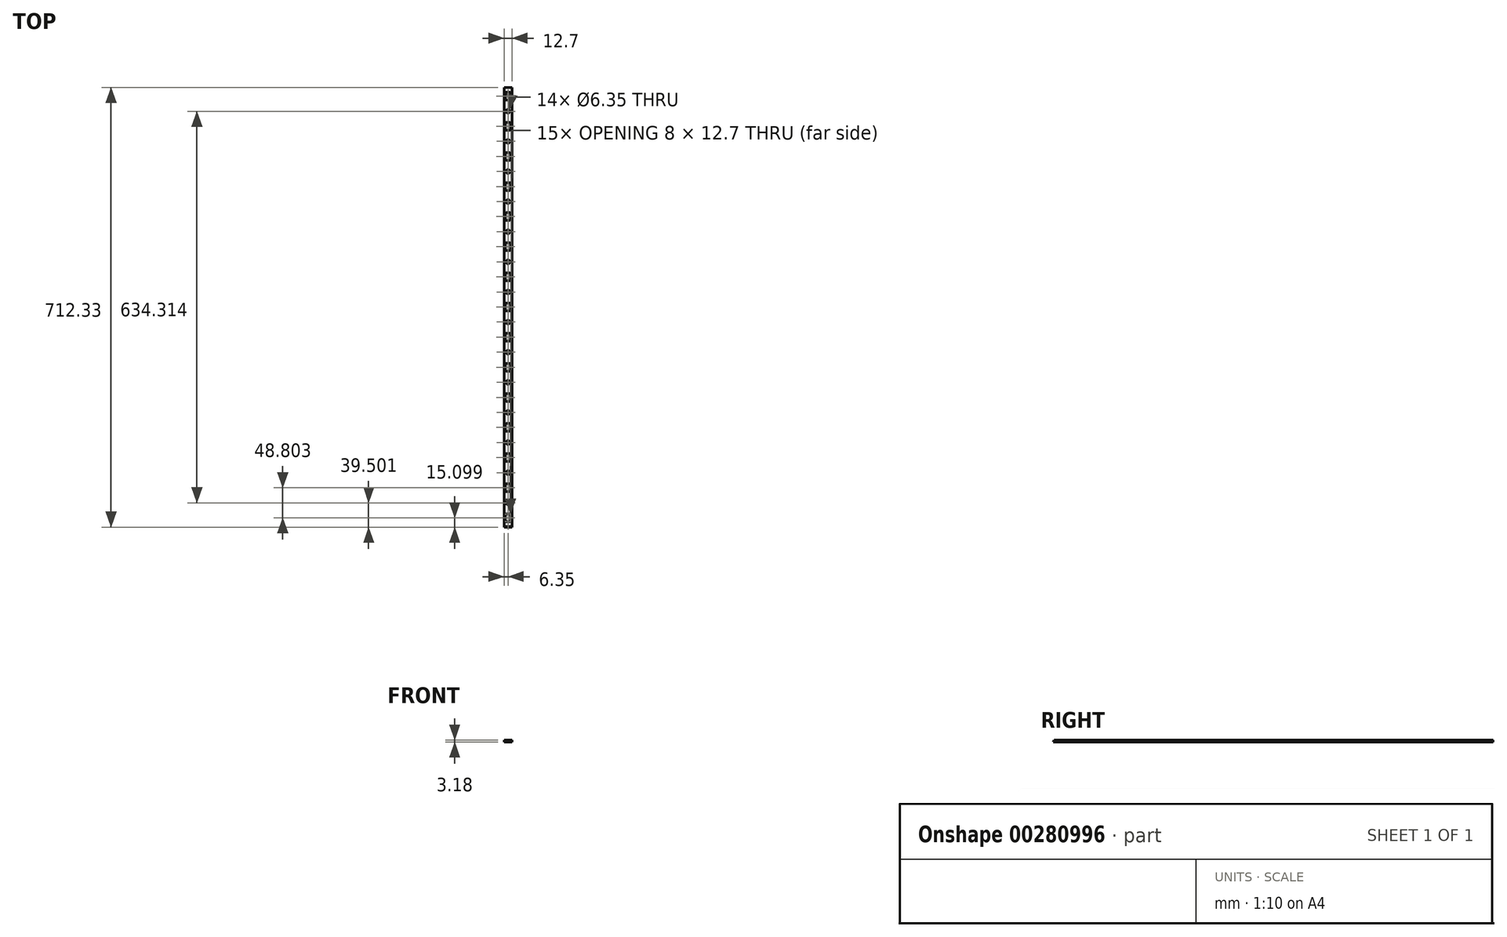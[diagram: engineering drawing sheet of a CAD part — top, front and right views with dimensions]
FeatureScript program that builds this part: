
annotation { "Feature Type Name" : "Feature", "Feature Type Description" : "" }
export const myFeature = defineFeature(function(context is Context, id is Id, definition is map)
    precondition{}
    {
        {
            var Q0;
            Q0=qCreatedBy(makeId("Right.planeOp"),FACE);
            var sketch = newSketch(context, id + "F0", { "sketchPlane" : qUnion([Q0])});
            skLineSegment(sketch, "E0", {"start": v(0, 0) * mm, "end": v(1.13, 3.17) * mm});
            skLineSegment(sketch, "E1", {"start": v(1.13, 3.18) * mm, "end": v(712.33, 3.18) * mm});
            skLineSegment(sketch, "E2", {"start": v(0, 0) * mm, "end": v(712.33, 0) * mm});
            skLineSegment(sketch, "E3", {"start": v(712.33, 3.18) * mm, "end": v(712.33, 0) * mm});
            skSolve(sketch);
        }
        {
            var Q0;
            Q0 = qSketchRegion(id + "F0", true);
            extrude(context, id + "F1", {"entities" : qUnion([Q0]), "oppositeDirection" : true, "depth" : 12.7 * mm});
        }
        {
            var Q0;
            Q0=makeQuery(id+"F1.opExtrude","SWEPT_FACE",FACE,{"disambiguationData":[OSD([sQuery(id+"F0.wireOp",EDGE,"E1")])]});
            var sketch = newSketch(context, id + "F2", { "sketchPlane" : qUnion([Q0])});
            skLineSegment(sketch, "E4.bottom", {"start": v(-3.62, 8.75) * mm, "end": v(-9.08, 8.75) * mm});
            skLineSegment(sketch, "E4.top", {"start": v(-3.62, 21.45) * mm, "end": v(-9.08, 21.45) * mm});
            skLineSegment(sketch, "E4.left", {"start": v(-2.35, 10.02) * mm, "end": v(-2.35, 20.18) * mm});
            skLineSegment(sketch, "E4.right", {"start": v(-10.35, 10.02) * mm, "end": v(-10.35, 20.18) * mm});
            skPoint(sketch, "E4.middle", {"position": v(-6.35, 15.1) * mm});
            skPoint(sketch, "E4.middle.positionSnap0", {"position": v(-6.35, 1.13) * mm});
            skPoint(sketch, "E4.centerSnap0", {"position": v(-6.35, 1.13) * mm});
            skPoint(sketch, "E5.visualSharp", {"position": v(-2.35, 21.45) * mm});
            skArc(sketch, "E5.filletArc", {"start": v(-2.35, 20.18) * mm, "mid": v(-2.72, 21.08) * mm, "end": v(-3.62, 21.45) * mm});
            skPoint(sketch, "E6.visualSharp", {"position": v(-10.35, 21.45) * mm});
            skArc(sketch, "E6.filletArc", {"start": v(-9.08, 21.45) * mm, "mid": v(-9.98, 21.08) * mm, "end": v(-10.35, 20.18) * mm});
            skPoint(sketch, "E7.visualSharp", {"position": v(-2.35, 8.75) * mm});
            skArc(sketch, "E7.filletArc", {"start": v(-3.62, 8.75) * mm, "mid": v(-2.72, 9.12) * mm, "end": v(-2.35, 10.02) * mm});
            skPoint(sketch, "E8.visualSharp", {"position": v(-10.35, 8.75) * mm});
            skArc(sketch, "E8.filletArc", {"start": v(-10.35, 10.02) * mm, "mid": v(-9.98, 9.12) * mm, "end": v(-9.08, 8.75) * mm});
            skArc(sketch, "E9.0.1.0", {"start": v(-3.62, 57.55) * mm, "mid": v(-2.72, 57.92) * mm, "end": v(-2.35, 58.82) * mm});
            skLineSegment(sketch, "E9.0.1.1", {"start": v(-10.35, 58.82) * mm, "end": v(-10.35, 68.98) * mm});
            skLineSegment(sketch, "E9.0.1.2", {"start": v(-3.62, 57.55) * mm, "end": v(-9.08, 57.55) * mm});
            skLineSegment(sketch, "E9.0.1.3", {"start": v(-2.35, 58.82) * mm, "end": v(-2.35, 68.98) * mm});
            skArc(sketch, "E9.0.1.4", {"start": v(-2.35, 68.98) * mm, "mid": v(-2.72, 69.88) * mm, "end": v(-3.62, 70.25) * mm});
            skLineSegment(sketch, "E9.0.1.5", {"start": v(-3.62, 70.25) * mm, "end": v(-9.08, 70.25) * mm});
            skArc(sketch, "E9.0.1.6", {"start": v(-9.08, 70.25) * mm, "mid": v(-9.98, 69.88) * mm, "end": v(-10.35, 68.98) * mm});
            skArc(sketch, "E9.0.1.7", {"start": v(-10.35, 58.82) * mm, "mid": v(-9.98, 57.92) * mm, "end": v(-9.08, 57.55) * mm});
            skArc(sketch, "E9.0.2.0", {"start": v(-3.62, 106.36) * mm, "mid": v(-2.72, 106.73) * mm, "end": v(-2.35, 107.63) * mm});
            skLineSegment(sketch, "E9.0.2.1", {"start": v(-10.35, 107.63) * mm, "end": v(-10.35, 117.79) * mm});
            skLineSegment(sketch, "E9.0.2.2", {"start": v(-3.62, 106.36) * mm, "end": v(-9.08, 106.36) * mm});
            skLineSegment(sketch, "E9.0.2.3", {"start": v(-2.35, 107.63) * mm, "end": v(-2.35, 117.79) * mm});
            skArc(sketch, "E9.0.2.4", {"start": v(-2.35, 117.79) * mm, "mid": v(-2.72, 118.68) * mm, "end": v(-3.62, 119.06) * mm});
            skLineSegment(sketch, "E9.0.2.5", {"start": v(-3.62, 119.06) * mm, "end": v(-9.08, 119.06) * mm});
            skArc(sketch, "E9.0.2.6", {"start": v(-9.08, 119.06) * mm, "mid": v(-9.98, 118.68) * mm, "end": v(-10.35, 117.79) * mm});
            skArc(sketch, "E9.0.2.7", {"start": v(-10.35, 107.63) * mm, "mid": v(-9.98, 106.73) * mm, "end": v(-9.08, 106.36) * mm});
            skArc(sketch, "E9.0.3.0", {"start": v(-3.62, 155.16) * mm, "mid": v(-2.72, 155.53) * mm, "end": v(-2.35, 156.43) * mm});
            skLineSegment(sketch, "E9.0.3.1", {"start": v(-10.35, 156.43) * mm, "end": v(-10.35, 166.59) * mm});
            skLineSegment(sketch, "E9.0.3.2", {"start": v(-3.62, 155.16) * mm, "end": v(-9.08, 155.16) * mm});
            skLineSegment(sketch, "E9.0.3.3", {"start": v(-2.35, 156.43) * mm, "end": v(-2.35, 166.59) * mm});
            skArc(sketch, "E9.0.3.4", {"start": v(-2.35, 166.59) * mm, "mid": v(-2.72, 167.49) * mm, "end": v(-3.62, 167.86) * mm});
            skLineSegment(sketch, "E9.0.3.5", {"start": v(-3.62, 167.86) * mm, "end": v(-9.08, 167.86) * mm});
            skArc(sketch, "E9.0.3.6", {"start": v(-9.08, 167.86) * mm, "mid": v(-9.98, 167.49) * mm, "end": v(-10.35, 166.59) * mm});
            skArc(sketch, "E9.0.3.7", {"start": v(-10.35, 156.43) * mm, "mid": v(-9.98, 155.53) * mm, "end": v(-9.08, 155.16) * mm});
            skArc(sketch, "E9.0.4.0", {"start": v(-3.62, 203.96) * mm, "mid": v(-2.72, 204.34) * mm, "end": v(-2.35, 205.23) * mm});
            skLineSegment(sketch, "E9.0.4.1", {"start": v(-10.35, 205.23) * mm, "end": v(-10.35, 215.4) * mm});
            skLineSegment(sketch, "E9.0.4.2", {"start": v(-3.62, 203.96) * mm, "end": v(-9.08, 203.96) * mm});
            skLineSegment(sketch, "E9.0.4.3", {"start": v(-2.35, 205.23) * mm, "end": v(-2.35, 215.4) * mm});
            skArc(sketch, "E9.0.4.4", {"start": v(-2.35, 215.4) * mm, "mid": v(-2.72, 216.3) * mm, "end": v(-3.62, 216.66) * mm});
            skLineSegment(sketch, "E9.0.4.5", {"start": v(-3.62, 216.66) * mm, "end": v(-9.08, 216.66) * mm});
            skArc(sketch, "E9.0.4.6", {"start": v(-9.08, 216.66) * mm, "mid": v(-9.98, 216.3) * mm, "end": v(-10.35, 215.4) * mm});
            skArc(sketch, "E9.0.4.7", {"start": v(-10.35, 205.23) * mm, "mid": v(-9.98, 204.34) * mm, "end": v(-9.08, 203.96) * mm});
            skArc(sketch, "E9.0.5.0", {"start": v(-3.62, 252.77) * mm, "mid": v(-2.72, 253.14) * mm, "end": v(-2.35, 254.04) * mm});
            skLineSegment(sketch, "E9.0.5.1", {"start": v(-10.35, 254.04) * mm, "end": v(-10.35, 264.2) * mm});
            skLineSegment(sketch, "E9.0.5.2", {"start": v(-3.62, 252.77) * mm, "end": v(-9.08, 252.77) * mm});
            skLineSegment(sketch, "E9.0.5.3", {"start": v(-2.35, 254.04) * mm, "end": v(-2.35, 264.2) * mm});
            skArc(sketch, "E9.0.5.4", {"start": v(-2.35, 264.2) * mm, "mid": v(-2.72, 265.1) * mm, "end": v(-3.62, 265.47) * mm});
            skLineSegment(sketch, "E9.0.5.5", {"start": v(-3.62, 265.47) * mm, "end": v(-9.08, 265.47) * mm});
            skArc(sketch, "E9.0.5.6", {"start": v(-9.08, 265.47) * mm, "mid": v(-9.98, 265.1) * mm, "end": v(-10.35, 264.2) * mm});
            skArc(sketch, "E9.0.5.7", {"start": v(-10.35, 254.04) * mm, "mid": v(-9.98, 253.14) * mm, "end": v(-9.08, 252.77) * mm});
            skArc(sketch, "E9.0.6.0", {"start": v(-3.62, 301.57) * mm, "mid": v(-2.72, 301.94) * mm, "end": v(-2.35, 302.84) * mm});
            skLineSegment(sketch, "E9.0.6.1", {"start": v(-10.35, 302.84) * mm, "end": v(-10.35, 313) * mm});
            skLineSegment(sketch, "E9.0.6.2", {"start": v(-3.62, 301.57) * mm, "end": v(-9.08, 301.57) * mm});
            skLineSegment(sketch, "E9.0.6.3", {"start": v(-2.35, 302.84) * mm, "end": v(-2.35, 313) * mm});
            skArc(sketch, "E9.0.6.4", {"start": v(-2.35, 313) * mm, "mid": v(-2.72, 313.9) * mm, "end": v(-3.62, 314.27) * mm});
            skLineSegment(sketch, "E9.0.6.5", {"start": v(-3.62, 314.27) * mm, "end": v(-9.08, 314.27) * mm});
            skArc(sketch, "E9.0.6.6", {"start": v(-9.08, 314.27) * mm, "mid": v(-9.98, 313.9) * mm, "end": v(-10.35, 313) * mm});
            skArc(sketch, "E9.0.6.7", {"start": v(-10.35, 302.84) * mm, "mid": v(-9.98, 301.94) * mm, "end": v(-9.08, 301.57) * mm});
            skArc(sketch, "E9.0.7.0", {"start": v(-3.62, 350.37) * mm, "mid": v(-2.72, 350.75) * mm, "end": v(-2.35, 351.64) * mm});
            skLineSegment(sketch, "E9.0.7.1", {"start": v(-10.35, 351.64) * mm, "end": v(-10.35, 361.8) * mm});
            skLineSegment(sketch, "E9.0.7.2", {"start": v(-3.62, 350.37) * mm, "end": v(-9.08, 350.37) * mm});
            skLineSegment(sketch, "E9.0.7.3", {"start": v(-2.35, 351.64) * mm, "end": v(-2.35, 361.8) * mm});
            skArc(sketch, "E9.0.7.4", {"start": v(-2.35, 361.8) * mm, "mid": v(-2.72, 362.7) * mm, "end": v(-3.62, 363.07) * mm});
            skLineSegment(sketch, "E9.0.7.5", {"start": v(-3.62, 363.07) * mm, "end": v(-9.08, 363.07) * mm});
            skArc(sketch, "E9.0.7.6", {"start": v(-9.08, 363.07) * mm, "mid": v(-9.98, 362.7) * mm, "end": v(-10.35, 361.8) * mm});
            skArc(sketch, "E9.0.7.7", {"start": v(-10.35, 351.64) * mm, "mid": v(-9.98, 350.75) * mm, "end": v(-9.08, 350.37) * mm});
            skArc(sketch, "E9.0.8.0", {"start": v(-3.62, 399.18) * mm, "mid": v(-2.72, 399.55) * mm, "end": v(-2.35, 400.45) * mm});
            skLineSegment(sketch, "E9.0.8.1", {"start": v(-10.35, 400.45) * mm, "end": v(-10.35, 410.6) * mm});
            skLineSegment(sketch, "E9.0.8.2", {"start": v(-3.62, 399.18) * mm, "end": v(-9.08, 399.18) * mm});
            skLineSegment(sketch, "E9.0.8.3", {"start": v(-2.35, 400.45) * mm, "end": v(-2.35, 410.6) * mm});
            skArc(sketch, "E9.0.8.4", {"start": v(-2.35, 410.6) * mm, "mid": v(-2.72, 411.5) * mm, "end": v(-3.62, 411.88) * mm});
            skLineSegment(sketch, "E9.0.8.5", {"start": v(-3.62, 411.88) * mm, "end": v(-9.08, 411.88) * mm});
            skArc(sketch, "E9.0.8.6", {"start": v(-9.08, 411.88) * mm, "mid": v(-9.98, 411.5) * mm, "end": v(-10.35, 410.6) * mm});
            skArc(sketch, "E9.0.8.7", {"start": v(-10.35, 400.45) * mm, "mid": v(-9.98, 399.55) * mm, "end": v(-9.08, 399.18) * mm});
            skArc(sketch, "E9.0.9.0", {"start": v(-3.62, 447.98) * mm, "mid": v(-2.72, 448.35) * mm, "end": v(-2.35, 449.25) * mm});
            skLineSegment(sketch, "E9.0.9.1", {"start": v(-10.35, 449.25) * mm, "end": v(-10.35, 459.41) * mm});
            skLineSegment(sketch, "E9.0.9.2", {"start": v(-3.62, 447.98) * mm, "end": v(-9.08, 447.98) * mm});
            skLineSegment(sketch, "E9.0.9.3", {"start": v(-2.35, 449.25) * mm, "end": v(-2.35, 459.41) * mm});
            skArc(sketch, "E9.0.9.4", {"start": v(-2.35, 459.41) * mm, "mid": v(-2.72, 460.3) * mm, "end": v(-3.62, 460.68) * mm});
            skLineSegment(sketch, "E9.0.9.5", {"start": v(-3.62, 460.68) * mm, "end": v(-9.08, 460.68) * mm});
            skArc(sketch, "E9.0.9.6", {"start": v(-9.08, 460.68) * mm, "mid": v(-9.98, 460.3) * mm, "end": v(-10.35, 459.41) * mm});
            skArc(sketch, "E9.0.9.7", {"start": v(-10.35, 449.25) * mm, "mid": v(-9.98, 448.35) * mm, "end": v(-9.08, 447.98) * mm});
            skArc(sketch, "E9.0.10.0", {"start": v(-3.62, 496.78) * mm, "mid": v(-2.72, 497.16) * mm, "end": v(-2.35, 498.05) * mm});
            skLineSegment(sketch, "E9.0.10.1", {"start": v(-10.35, 498.05) * mm, "end": v(-10.35, 508.21) * mm});
            skLineSegment(sketch, "E9.0.10.2", {"start": v(-3.62, 496.78) * mm, "end": v(-9.08, 496.78) * mm});
            skLineSegment(sketch, "E9.0.10.3", {"start": v(-2.35, 498.05) * mm, "end": v(-2.35, 508.21) * mm});
            skArc(sketch, "E9.0.10.4", {"start": v(-2.35, 508.21) * mm, "mid": v(-2.72, 509.11) * mm, "end": v(-3.62, 509.48) * mm});
            skLineSegment(sketch, "E9.0.10.5", {"start": v(-3.62, 509.48) * mm, "end": v(-9.08, 509.48) * mm});
            skArc(sketch, "E9.0.10.6", {"start": v(-9.08, 509.48) * mm, "mid": v(-9.98, 509.11) * mm, "end": v(-10.35, 508.21) * mm});
            skArc(sketch, "E9.0.10.7", {"start": v(-10.35, 498.05) * mm, "mid": v(-9.98, 497.16) * mm, "end": v(-9.08, 496.78) * mm});
            skArc(sketch, "E9.0.11.0", {"start": v(-3.62, 545.59) * mm, "mid": v(-2.72, 545.96) * mm, "end": v(-2.35, 546.86) * mm});
            skLineSegment(sketch, "E9.0.11.1", {"start": v(-10.35, 546.86) * mm, "end": v(-10.35, 557.02) * mm});
            skLineSegment(sketch, "E9.0.11.2", {"start": v(-3.62, 545.59) * mm, "end": v(-9.08, 545.59) * mm});
            skLineSegment(sketch, "E9.0.11.3", {"start": v(-2.35, 546.86) * mm, "end": v(-2.35, 557.02) * mm});
            skArc(sketch, "E9.0.11.4", {"start": v(-2.35, 557.02) * mm, "mid": v(-2.72, 557.92) * mm, "end": v(-3.62, 558.29) * mm});
            skLineSegment(sketch, "E9.0.11.5", {"start": v(-3.62, 558.29) * mm, "end": v(-9.08, 558.29) * mm});
            skArc(sketch, "E9.0.11.6", {"start": v(-9.08, 558.29) * mm, "mid": v(-9.98, 557.92) * mm, "end": v(-10.35, 557.02) * mm});
            skArc(sketch, "E9.0.11.7", {"start": v(-10.35, 546.86) * mm, "mid": v(-9.98, 545.96) * mm, "end": v(-9.08, 545.59) * mm});
            skArc(sketch, "E9.0.12.0", {"start": v(-3.62, 594.4) * mm, "mid": v(-2.72, 594.76) * mm, "end": v(-2.35, 595.66) * mm});
            skLineSegment(sketch, "E9.0.12.1", {"start": v(-10.35, 595.66) * mm, "end": v(-10.35, 605.82) * mm});
            skLineSegment(sketch, "E9.0.12.2", {"start": v(-3.62, 594.4) * mm, "end": v(-9.08, 594.4) * mm});
            skLineSegment(sketch, "E9.0.12.3", {"start": v(-2.35, 595.66) * mm, "end": v(-2.35, 605.82) * mm});
            skArc(sketch, "E9.0.12.4", {"start": v(-2.35, 605.82) * mm, "mid": v(-2.72, 606.72) * mm, "end": v(-3.62, 607.1) * mm});
            skLineSegment(sketch, "E9.0.12.5", {"start": v(-3.62, 607.1) * mm, "end": v(-9.08, 607.1) * mm});
            skArc(sketch, "E9.0.12.6", {"start": v(-9.08, 607.1) * mm, "mid": v(-9.98, 606.72) * mm, "end": v(-10.35, 605.82) * mm});
            skArc(sketch, "E9.0.12.7", {"start": v(-10.35, 595.66) * mm, "mid": v(-9.98, 594.76) * mm, "end": v(-9.08, 594.4) * mm});
            skArc(sketch, "E9.0.13.0", {"start": v(-3.62, 643.2) * mm, "mid": v(-2.72, 643.57) * mm, "end": v(-2.35, 644.47) * mm});
            skLineSegment(sketch, "E9.0.13.1", {"start": v(-10.35, 644.47) * mm, "end": v(-10.35, 654.63) * mm});
            skLineSegment(sketch, "E9.0.13.2", {"start": v(-3.62, 643.2) * mm, "end": v(-9.08, 643.2) * mm});
            skLineSegment(sketch, "E9.0.13.3", {"start": v(-2.35, 644.47) * mm, "end": v(-2.35, 654.63) * mm});
            skArc(sketch, "E9.0.13.4", {"start": v(-2.35, 654.63) * mm, "mid": v(-2.72, 655.52) * mm, "end": v(-3.62, 655.9) * mm});
            skLineSegment(sketch, "E9.0.13.5", {"start": v(-3.62, 655.9) * mm, "end": v(-9.08, 655.9) * mm});
            skArc(sketch, "E9.0.13.6", {"start": v(-9.08, 655.9) * mm, "mid": v(-9.98, 655.52) * mm, "end": v(-10.35, 654.63) * mm});
            skArc(sketch, "E9.0.13.7", {"start": v(-10.35, 644.47) * mm, "mid": v(-9.98, 643.57) * mm, "end": v(-9.08, 643.2) * mm});
            skArc(sketch, "E9.0.14.0", {"start": v(-3.62, 692) * mm, "mid": v(-2.72, 692.37) * mm, "end": v(-2.35, 693.27) * mm});
            skLineSegment(sketch, "E9.0.14.1", {"start": v(-10.35, 693.27) * mm, "end": v(-10.35, 703.43) * mm});
            skLineSegment(sketch, "E9.0.14.2", {"start": v(-3.62, 692) * mm, "end": v(-9.08, 692) * mm});
            skLineSegment(sketch, "E9.0.14.3", {"start": v(-2.35, 693.27) * mm, "end": v(-2.35, 703.43) * mm});
            skArc(sketch, "E9.0.14.4", {"start": v(-2.35, 703.43) * mm, "mid": v(-2.72, 704.33) * mm, "end": v(-3.62, 704.7) * mm});
            skLineSegment(sketch, "E9.0.14.5", {"start": v(-3.62, 704.7) * mm, "end": v(-9.08, 704.7) * mm});
            skArc(sketch, "E9.0.14.6", {"start": v(-9.08, 704.7) * mm, "mid": v(-9.98, 704.33) * mm, "end": v(-10.35, 703.43) * mm});
            skArc(sketch, "E9.0.14.7", {"start": v(-10.35, 693.27) * mm, "mid": v(-9.98, 692.37) * mm, "end": v(-9.08, 692) * mm});
            skLineSegment(sketch, "E9.direction1", {"start": v(-2.35, 10.02) * mm, "end": v(23.05, 10.02) * mm, "construction": true});
            skLineSegment(sketch, "E9.direction2", {"start": v(-2.35, 10.02) * mm, "end": v(-2.35, 58.82) * mm, "construction": true});
            skSolve(sketch);
        }
        {
            var Q0;
            Q0 = qSketchRegion(id + "F2", true);
            var Q1;
            Q1=makeQuery(id+"F1.opExtrude","SWEPT_FACE",FACE,{"disambiguationData":[OSD([sQuery(id+"F0.wireOp",EDGE,"E2")])]});
            extrude(context, id + "F3", {"entities" : qUnion([Q0]), "operationType" : NewBodyOperationType.REMOVE, "endBound" : BoundingType.UP_TO_SURFACE, "oppositeDirection" : true, "endBoundEntityFace" : qUnion([Q1]), "depth" : 25.4 * mm});
        }
        {
            var Q0;
            Q0=makeQuery(id+"F1.opExtrude","SWEPT_FACE",FACE,{"disambiguationData":[OSD([sQuery(id+"F0.wireOp",EDGE,"E1")])]});
            var sketch = newSketch(context, id + "F4", { "sketchPlane" : qUnion([Q0])});
            skLineSegment(sketch, "E10", {"start": v(-6.35, 57.55) * mm, "end": v(-6.35, 21.45) * mm, "construction": true});
            skLineSegment(sketch, "E11", {"start": v(-6.35, 39.5) * mm, "end": v(6.94, 39.5) * mm, "construction": true});
            skCircle(sketch, "E12", {"center": v(-6.35, 39.5) * mm, "radius": 3.18 * mm});
            skCircle(sketch, "E13.0.1.0", {"center": v(-6.35, 88.3) * mm, "radius": 3.18 * mm});
            skCircle(sketch, "E13.0.2.0", {"center": v(-6.35, 137.09) * mm, "radius": 3.18 * mm});
            skCircle(sketch, "E13.0.3.0", {"center": v(-6.35, 185.88) * mm, "radius": 3.18 * mm});
            skCircle(sketch, "E13.0.4.0", {"center": v(-6.35, 234.67) * mm, "radius": 3.18 * mm});
            skCircle(sketch, "E13.0.5.0", {"center": v(-6.35, 283.47) * mm, "radius": 3.18 * mm});
            skCircle(sketch, "E13.0.6.0", {"center": v(-6.35, 332.26) * mm, "radius": 3.18 * mm});
            skCircle(sketch, "E13.0.7.0", {"center": v(-6.35, 381.05) * mm, "radius": 3.18 * mm});
            skCircle(sketch, "E13.0.8.0", {"center": v(-6.35, 429.85) * mm, "radius": 3.18 * mm});
            skCircle(sketch, "E13.0.9.0", {"center": v(-6.35, 478.64) * mm, "radius": 3.18 * mm});
            skCircle(sketch, "E13.0.10.0", {"center": v(-6.35, 527.43) * mm, "radius": 3.18 * mm});
            skCircle(sketch, "E13.0.11.0", {"center": v(-6.35, 576.23) * mm, "radius": 3.18 * mm});
            skCircle(sketch, "E13.0.12.0", {"center": v(-6.35, 625.02) * mm, "radius": 3.18 * mm});
            skCircle(sketch, "E13.0.13.0", {"center": v(-6.35, 673.81) * mm, "radius": 3.18 * mm});
            skLineSegment(sketch, "E13.direction1", {"start": v(-6.35, 39.5) * mm, "end": v(19.05, 39.5) * mm, "construction": true});
            skLineSegment(sketch, "E13.direction2", {"start": v(-6.35, 39.5) * mm, "end": v(-6.35, 88.3) * mm, "construction": true});
            skSolve(sketch);
        }
        {
            var Q0;
            Q0 = qSketchRegion(id + "F4", true);
            var Q1;
            Q1=makeQuery(id+"F1.opExtrude","SWEPT_FACE",FACE,{"disambiguationData":[OSD([sQuery(id+"F0.wireOp",EDGE,"E2")])]});
            extrude(context, id + "F5", {"entities" : qUnion([Q0]), "operationType" : NewBodyOperationType.REMOVE, "endBound" : BoundingType.UP_TO_SURFACE, "oppositeDirection" : true, "endBoundEntityFace" : qUnion([Q1]), "depth" : 25.4 * mm});
        }
    });
